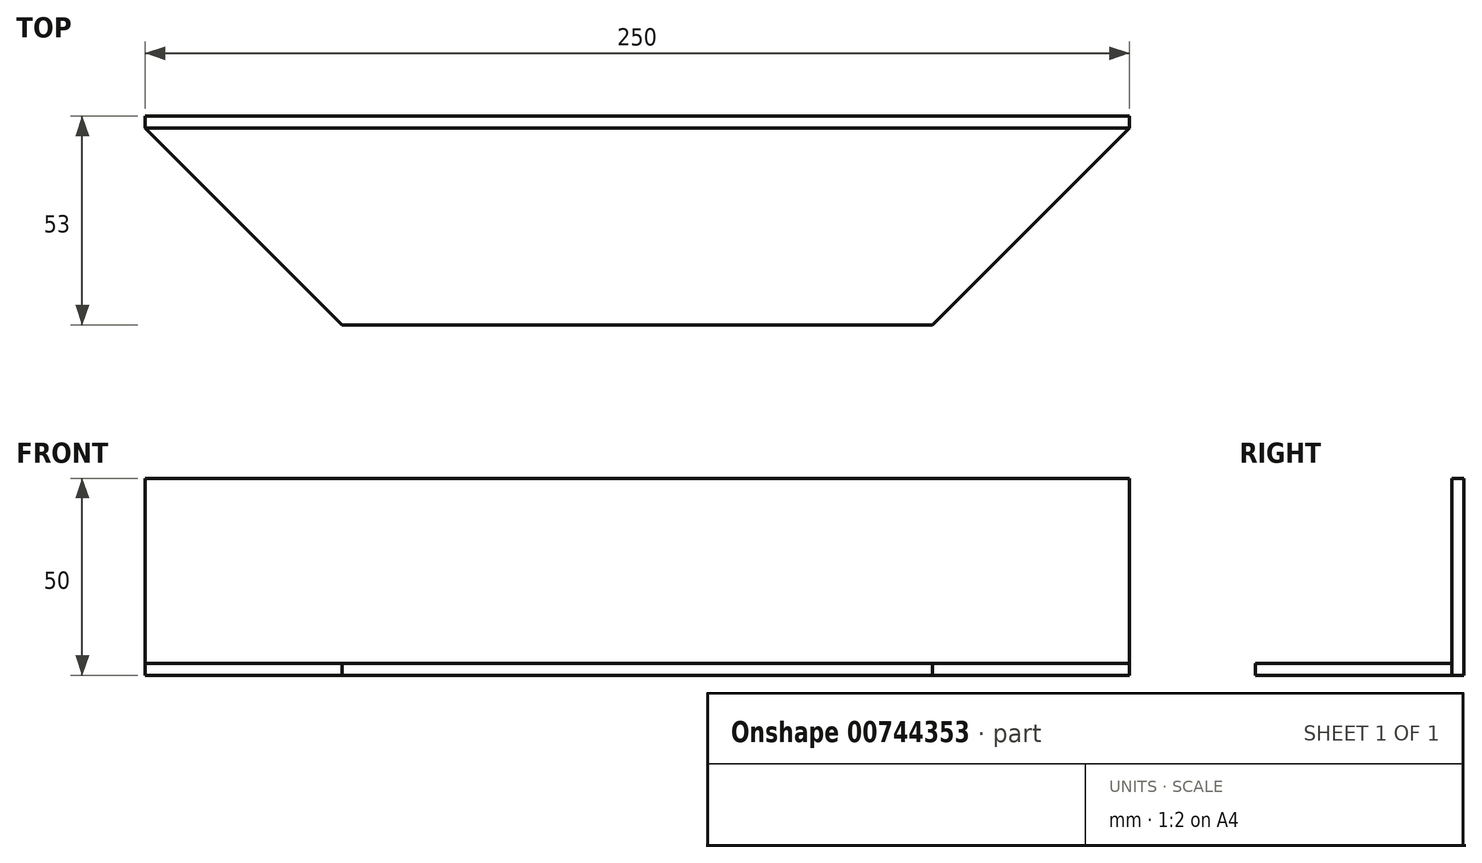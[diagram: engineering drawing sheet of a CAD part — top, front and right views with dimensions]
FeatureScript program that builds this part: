
annotation { "Feature Type Name" : "Feature", "Feature Type Description" : "" }
export const myFeature = defineFeature(function(context is Context, id is Id, definition is map)
    precondition{}
    {
        {
            var Q0;
            Q0=qCreatedBy(makeId("Top.planeOp"),FACE);
            var sketch = newSketch(context, id + "F0", { "sketchPlane" : qUnion([Q0])});
            skLineSegment(sketch, "E0.bottom", {"start": v(-75, -25) * mm, "end": v(75, -25) * mm});
            skLineSegment(sketch, "E0.top", {"start": v(-125, 25) * mm, "end": v(125, 25) * mm});
            skPoint(sketch, "E0.middle", {"position": v(0, 0) * mm});
            skLineSegment(sketch, "E1", {"start": v(0, -25) * mm, "end": v(-75, -25) * mm});
            skLineSegment(sketch, "E2", {"start": v(-75, -25) * mm, "end": v(-125, 25) * mm});
            skLineSegment(sketch, "E3", {"start": v(0, -25) * mm, "end": v(75, -25) * mm});
            skLineSegment(sketch, "E4", {"start": v(75, -25) * mm, "end": v(125, 25) * mm});
            skPoint(sketch, "E5.orphan", {"position": v(-125, -25) * mm});
            skPoint(sketch, "E6.orphan", {"position": v(125, -25) * mm});
            skLineSegment(sketch, "E7", {"start": v(-125, 25) * mm, "end": v(-125, 28) * mm});
            skLineSegment(sketch, "E8", {"start": v(125, 25) * mm, "end": v(125, 28) * mm});
            skLineSegment(sketch, "E9", {"start": v(125, 28) * mm, "end": v(-125, 28) * mm});
            skSolve(sketch);
        }
        {
            var Q0;
            Q0=makeQuery(id+"F0.imprint","IMPRINT",FACE,{"disambiguationData":[TD([[makeQuery(id+"F0.imprint","IMPRINT",EDGE,{"derivedFrom":sQuery(id+"F0.wireOp",EDGE,"E0.top")}),1.0]])]});
            extrude(context, id + "F1", {"entities" : qUnion([Q0]), "depth" : 50 * mm, "offsetDistance" : 25 * mm});
        }
        {
            var Q0;
            Q0=makeQuery(id+"F0.imprint","IMPRINT",FACE,{"disambiguationData":[TD([[makeQuery(id+"F0.imprint","IMPRINT",EDGE,{"derivedFrom":sQuery(id+"F0.wireOp",EDGE,"E0.top")}),-1.0]])]});
            extrude(context, id + "F2", {"entities" : qUnion([Q0]), "operationType" : NewBodyOperationType.ADD, "depth" : 3 * mm, "offsetDistance" : 25 * mm});
        }
    });
